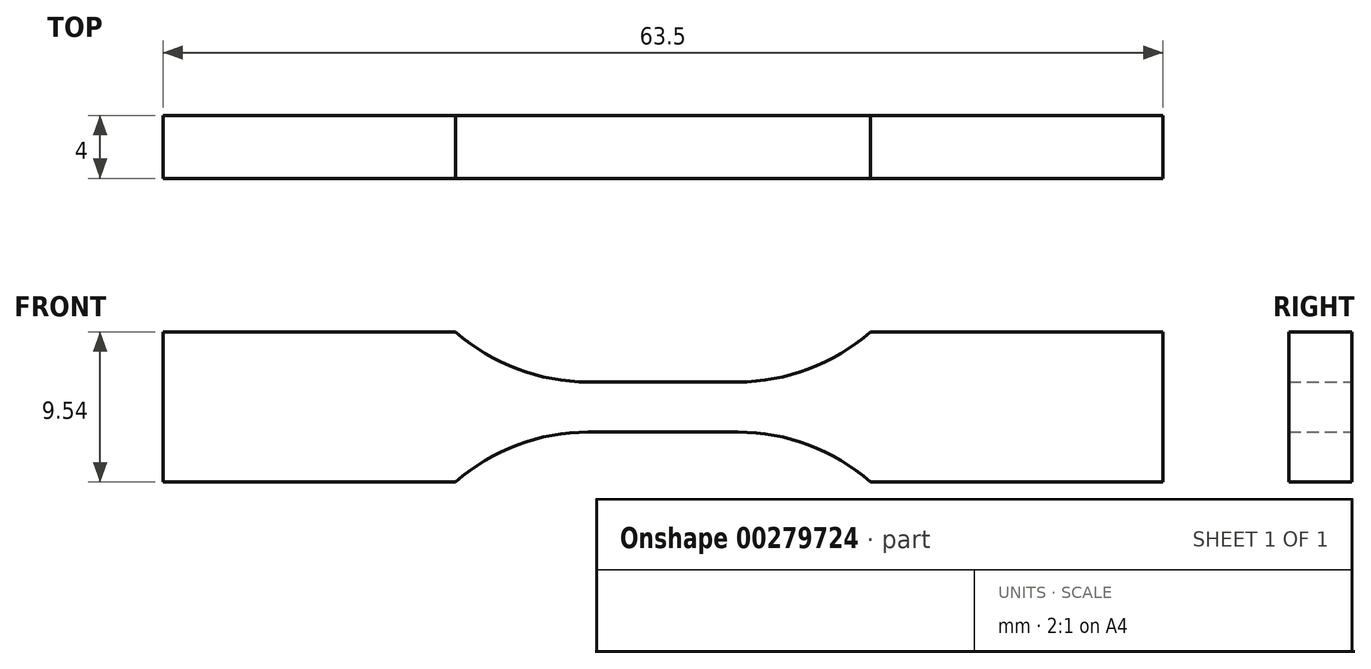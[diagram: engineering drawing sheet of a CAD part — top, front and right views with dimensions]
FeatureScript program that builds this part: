
annotation { "Feature Type Name" : "Feature", "Feature Type Description" : "" }
export const myFeature = defineFeature(function(context is Context, id is Id, definition is map)
    precondition{}
    {
        {
            var Q0;
            Q0=qCreatedBy(makeId("Front.planeOp"),FACE);
            var sketch = newSketch(context, id + "F0", { "sketchPlane" : qUnion([Q0])});
            skLineSegment(sketch, "E0", {"start": v(0, 1.6) * mm, "end": v(4.75, 1.6) * mm});
            skArc(sketch, "E1", {"start": v(4.75, 1.59) * mm, "mid": v(9.25, 2.41) * mm, "end": v(13.17, 4.77) * mm});
            skLineSegment(sketch, "E2", {"start": v(13.17, 4.77) * mm, "end": v(31.75, 4.77) * mm});
            skArc(sketch, "E3.MirrorCS", {"start": v(4.75, -1.59) * mm, "mid": v(9.25, -2.41) * mm, "end": v(13.17, -4.77) * mm});
            skLineSegment(sketch, "E4.MirrorCS", {"start": v(0, -1.59) * mm, "end": v(4.75, -1.59) * mm});
            skLineSegment(sketch, "E5.MirrorCS", {"start": v(13.17, -4.77) * mm, "end": v(31.75, -4.77) * mm});
            skLineSegment(sketch, "E6.MirrorCS", {"start": v(0, 1.59) * mm, "end": v(-4.75, 1.6) * mm});
            skArc(sketch, "E7.MirrorCS", {"start": v(-4.75, -1.59) * mm, "mid": v(-9.25, -2.41) * mm, "end": v(-13.17, -4.77) * mm});
            skArc(sketch, "E8.MirrorCS", {"start": v(-4.75, 1.59) * mm, "mid": v(-9.25, 2.41) * mm, "end": v(-13.17, 4.77) * mm});
            skLineSegment(sketch, "E9.MirrorCS", {"start": v(-13.17, 4.77) * mm, "end": v(-31.75, 4.77) * mm});
            skLineSegment(sketch, "E10.MirrorCS", {"start": v(0, -1.59) * mm, "end": v(-4.75, -1.59) * mm});
            skLineSegment(sketch, "E11.MirrorCS", {"start": v(-13.17, -4.77) * mm, "end": v(-31.75, -4.77) * mm});
            skLineSegment(sketch, "E12", {"start": v(-31.75, -4.77) * mm, "end": v(-31.75, 4.77) * mm});
            skLineSegment(sketch, "E13", {"start": v(31.75, -4.77) * mm, "end": v(31.75, 4.77) * mm});
            skSolve(sketch);
        }
        {
            var Q0;
            Q0=makeQuery(id+"F0.imprint","IMPRINT",FACE,{"disambiguationData":[TD([[makeQuery(id+"F0.imprint","IMPRINT",EDGE,{"derivedFrom":sQuery(id+"F0.wireOp",EDGE,"E0")}),-1.0]])]});
            extrude(context, id + "F1", {"entities" : qUnion([Q0]), "endBound" : BoundingType.SYMMETRIC, "depth" : 4 * mm});
        }
    });
